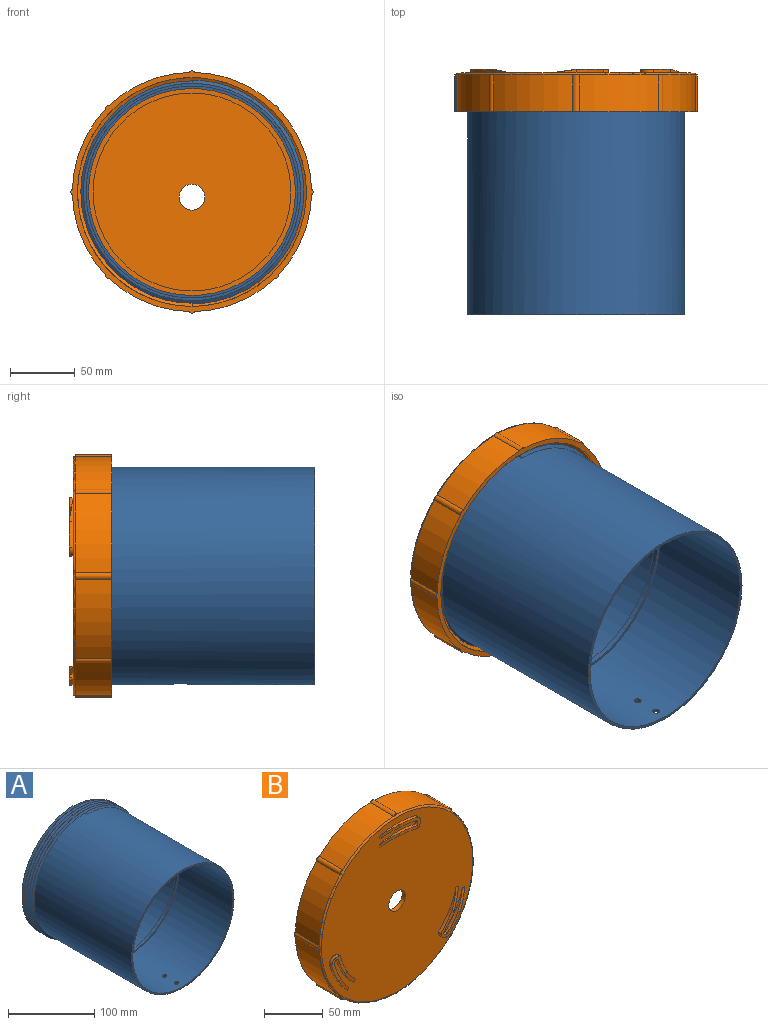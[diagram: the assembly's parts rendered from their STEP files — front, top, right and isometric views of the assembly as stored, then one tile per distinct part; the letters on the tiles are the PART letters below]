
ASSEMBLY  parts=2 mates=1
PART A: 20 faces, bbox 199.8x180x173 mm
  f0: cylinder r=84mm len=168mm, axis (0,1,0), area 83625.4mm2, adj f5,f8,f14,f15,f17,f18,f19
  f1: cylinder r=84mm len=168mm, axis (0,1,0), area 1055.6mm2, adj f2,f9,f13,f16
  f2: cylinder r=84mm len=168mm, axis (0,1,0), area 587.6mm2, adj f1,f3,f15,f16
  f3: cylinder r=84mm len=168mm, axis (0,1,0), area 587.6mm2, adj f2,f4,f15,f16
  f4: cylinder r=84mm len=168mm, axis (0,1,0), area 587.6mm2, adj f3,f5,f15,f16
  f5: cylinder r=84mm len=168mm, axis (0,1,0), area 587.6mm2, adj f0,f4,f15,f16
  f6: cylinder r=82mm len=164mm, axis (0,1,0), area 45300.5mm2, adj f8,f10,f18,f19
  f7: cylinder r=82mm len=164mm, axis (0,1,0), area 45025.2mm2, adj f9,f11,f17
  f8: plane 168x168mm, normal (0,-1,0), area 1043mm2, adj f0,f6
  f9: plane 168x168mm, normal (0,1,0), area 1043mm2, adj f1,f7
  f10: plane 164x164mm, normal (0,-1,0), area 1017.9mm2, adj f6,f12
  f11: plane 164x164mm, normal (0,1,0), area 1017.9mm2, adj f7,f12
  f12: cylinder r=80mm len=160mm, axis (0,1,0), area 2010.6mm2, adj f10,f11
  f13: plane 2.89x2.5mm, normal (1,0,0), area 3.6mm2, adj f1,f15,f16
  f14: plane 2.89x2.5mm, normal (-1,0,0), area 3.6mm2, adj f0,f15,f16
  f15: bspline ~199.76x173mm, area 7725.5mm2, adj f0,f2,f3,f4,f5,f13,f14,f16
  f16: bspline ~199.76x173mm, area 7731.3mm2, adj f1,f2,f3,f4,f5,f13,f14,f15
  f17: cylinder r=10mm len=20mm, axis (0,0,1), area 126.1mm2, adj f0,f7
  f18: cylinder r=2.5mm len=5mm, axis (0,0,1), area 31.4mm2, adj f0,f6
  f19: cylinder r=2.5mm len=5mm, axis (0,0,1), area 31.4mm2, adj f0,f6
PART B: 74 faces, bbox 207x35.6x202.9 mm
  f0: plane 182.02x182.02mm, normal (0,-1,0), area 24838.9mm2, adj f14,f35,f36,f37,f40,f41,f42,f43
  f1: cylinder r=92.5mm len=61.25mm, axis (0,1,0), area 1932.3mm2, adj f10,f14,f30,f32
  f2: cylinder r=92.5mm len=61.25mm, axis (0,1,0), area 1932.3mm2, adj f10,f14,f18,f32
  f3: cylinder r=92.5mm len=61.25mm, axis (0,1,0), area 1932.3mm2, adj f10,f14,f28,f30
  f4: cylinder r=92.5mm len=61.25mm, axis (0,1,0), area 1932.3mm2, adj f10,f14,f26,f28
  f5: cylinder r=92.5mm len=61.25mm, axis (0,1,0), area 1932.3mm2, adj f10,f14,f24,f26
  f6: cylinder r=92.5mm len=61.25mm, axis (0,1,0), area 1932.3mm2, adj f10,f14,f22,f24
  f7: cylinder r=92.5mm len=61.25mm, axis (0,1,0), area 1932.3mm2, adj f10,f14,f20,f22
  f8: cylinder r=92.5mm len=61.25mm, axis (0,1,0), area 1932.3mm2, adj f10,f14,f18,f20
  f9: cylinder r=88.5mm len=177mm, axis (0,1,0), area 5330.2mm2, adj f10,f11,f15,f16,f17
  f10: plane 187.4x187.4mm, normal (0,1,0), area 2307.2mm2, adj f1,f2,f3,f4,f5,f6,f7,f8
  f11: plane 178.62x177.65mm, normal (0,1,0), area 5788.2mm2, adj f9,f12,f16,f17
  f12: cylinder r=76.5mm len=153mm, axis (0,1,0), area 1442mm2, adj f11,f13
  f13: plane 153x153mm, normal (0,1,0), area 18071.2mm2, adj f12,f73
  f14: torus R=91mm, axis (0,-1,0), area 1361.3mm2, adj f0,f1,f2,f3,f4,f5,f6,f7
  f15: plane 2.89x2.5mm, normal (1,0,0), area 3.6mm2, adj f9,f16,f17
  f16: bspline ~204.38x177mm, area 7672.4mm2, adj f9,f11,f15,f17
  f17: bspline ~204.38x177mm, area 7173.2mm2, adj f9,f11,f15,f16
  f18: cylinder r=3mm len=28.5mm, axis (0,1,0), area 161mm2, adj f2,f8,f10,f19
  f19: plane 4.85x1.23mm, normal (0,-1,0), area 4.1mm2, adj f14,f18
  f20: cylinder r=3mm len=28.5mm, axis (0,1,0), area 161mm2, adj f7,f8,f10,f21
  f21: plane 3.47x3.47mm, normal (0,-1,0), area 4.1mm2, adj f14,f20
  f22: cylinder r=3mm len=28.5mm, axis (0,1,0), area 161mm2, adj f6,f7,f10,f23
  f23: plane 4.85x1.23mm, normal (0,-1,0), area 4.1mm2, adj f14,f22
  f24: cylinder r=3mm len=28.5mm, axis (0,1,0), area 161mm2, adj f5,f6,f10,f25
  f25: plane 3.47x3.47mm, normal (0,-1,0), area 4.1mm2, adj f14,f24
  f26: cylinder r=3mm len=28.5mm, axis (0,1,0), area 161mm2, adj f4,f5,f10,f27
  f27: plane 4.85x1.23mm, normal (0,-1,0), area 4.1mm2, adj f14,f26
  f28: cylinder r=3mm len=28.5mm, axis (0,1,0), area 161mm2, adj f3,f4,f10,f29
  f29: plane 3.47x3.47mm, normal (0,-1,0), area 4.1mm2, adj f14,f28
  f30: cylinder r=3mm len=28.5mm, axis (0,1,0), area 161mm2, adj f1,f3,f10,f31
  f31: plane 4.85x1.23mm, normal (0,-1,0), area 4.1mm2, adj f14,f30
  f32: cylinder r=3mm len=28.5mm, axis (0,1,0), area 161mm2, adj f1,f2,f10,f33
  f33: plane 3.47x3.47mm, normal (0,-1,0), area 4.1mm2, adj f14,f32
  f34: plane 25.24x14.65mm, normal (0,-1,0), area 160mm2, adj f35,f36,f37,f38,f39,f40,f41,f42
  f35: cylinder r=84.5mm len=21.38mm, axis (0,-1,0), area 32.5mm2, adj f0,f34,f37,f44
  f36: cylinder r=81.5mm len=41.06mm, axis (0,-1,0), area 92.2mm2, adj f0,f34,f37,f38,f42
  f37: plane 21.4x5.68mm, normal (-0.13,-0.99,-0.04), area 64.3mm2, adj f0,f34,f35,f36,f38
  f38: plane 2.87x0.1mm, normal (-1,0,0), area 0.1mm2, adj f34,f36,f37
  f39: plane 2.73x0.11mm, normal (-1,0,0), area 0.1mm2, adj f34,f41,f46
  f40: cylinder r=76mm len=42.19mm, axis (0,-1,0), area 95.8mm2, adj f0,f34,f42,f46
  f41: bspline ~21.32x3.18mm, area 64.4mm2, adj f0,f34,f39,f43,f45
  f42: cylinder r=3.5mm len=5.79mm, axis (0,1,0), area 20.5mm2, adj f0,f34,f36,f40
  f43: bspline ~11.97x4.12mm, area 44.5mm2, adj f0,f34,f41,f44
  f44: bspline ~21.66x3mm, area 65.4mm2, adj f0,f34,f35,f43
  f45: cylinder r=73mm len=20.58mm, axis (0,-1,0), area 30.2mm2, adj f0,f41,f46
  f46: plane 21.45x5.99mm, normal (-0.13,-0.99,-0.04), area 64.5mm2, adj f0,f34,f39,f40,f45
  f47: plane 27.01x18.36mm, normal (0,-1,0), area 160mm2, adj f48,f49,f50,f51,f52,f53,f54,f55
  f48: cylinder r=84.5mm len=17.14mm, axis (0,-1,0), area 32.5mm2, adj f0,f47,f50,f57
  f49: cylinder r=81.5mm len=35.53mm, axis (0,-1,0), area 92.2mm2, adj f0,f47,f50,f51,f55
  f50: plane 18.67x15.21mm, normal (0.1,-0.99,-0.1), area 64.3mm2, adj f0,f47,f48,f49,f51
  f51: plane 2.48x1.43mm, normal (0.5,0,-0.87), area 0.1mm2, adj f47,f49,f50
  f52: plane 2.36x1.36mm, normal (0.5,0,-0.87), area 0.1mm2, adj f47,f54,f59
  f53: cylinder r=76mm len=36.44mm, axis (0,-1,0), area 95.8mm2, adj f0,f47,f55,f59
  f54: bspline ~20.05x7.91mm, area 64.4mm2, adj f0,f47,f52,f56,f58
  f55: cylinder r=3.5mm len=4.85mm, axis (0,1,0), area 20.5mm2, adj f0,f47,f49,f53
  f56: bspline ~10.59x7.03mm, area 44.5mm2, adj f0,f47,f54,f57
  f57: bspline ~20.17x8.39mm, area 65.4mm2, adj f0,f47,f48,f56
  f58: cylinder r=73mm len=16.34mm, axis (0,-1,0), area 30.2mm2, adj f0,f54,f59
  f59: plane 18.54x15.44mm, normal (0.1,-0.99,-0.1), area 64.5mm2, adj f0,f47,f52,f53,f58
  f60: plane 24.12x23.33mm, normal (0,-1,0), area 160mm2, adj f61,f62,f63,f64,f65,f66,f67,f68
  f61: cylinder r=84.5mm len=19.89mm, axis (0,-1,0), area 32.5mm2, adj f0,f60,f63,f70
  f62: cylinder r=81.5mm len=35.58mm, axis (0,-1,0), area 92.2mm2, adj f0,f60,f63,f64,f68
  f63: plane 20.68x10.93mm, normal (0.04,-0.99,0.13), area 64.3mm2, adj f0,f60,f61,f62,f64
  f64: plane 2.48x1.43mm, normal (0.5,0,0.87), area 0.1mm2, adj f60,f62,f63
  f65: plane 2.36x1.36mm, normal (0.5,0,0.87), area 0.1mm2, adj f60,f67,f72
  f66: cylinder r=76mm len=36.63mm, axis (0,-1,0), area 95.8mm2, adj f0,f60,f68,f72
  f67: bspline ~16.88x13.41mm, area 64.4mm2, adj f0,f60,f65,f69,f71
  f68: cylinder r=3.5mm len=5.18mm, axis (0,1,0), area 20.5mm2, adj f0,f60,f62,f66
  f69: bspline ~10.19x7.51mm, area 44.5mm2, adj f0,f60,f67,f70
  f70: bspline ~17.35x13.28mm, area 65.4mm2, adj f0,f60,f61,f69
  f71: cylinder r=73mm len=19.3mm, axis (0,-1,0), area 30.2mm2, adj f0,f67,f72
  f72: plane 20.76x10.67mm, normal (0.03,-0.99,0.14), area 64.5mm2, adj f0,f60,f65,f66,f71
  f73: cylinder r=10mm len=20mm, axis (0,-1,0), area 251.3mm2, adj f0,f13
PLACE A at identity
PLACE B rot(axis=(1,0,0),180deg) t=(0,-23,0)mm
MATE fastened B.f1 <-> A.f0  axis (0,-1,0) through (0,0,0)mm
